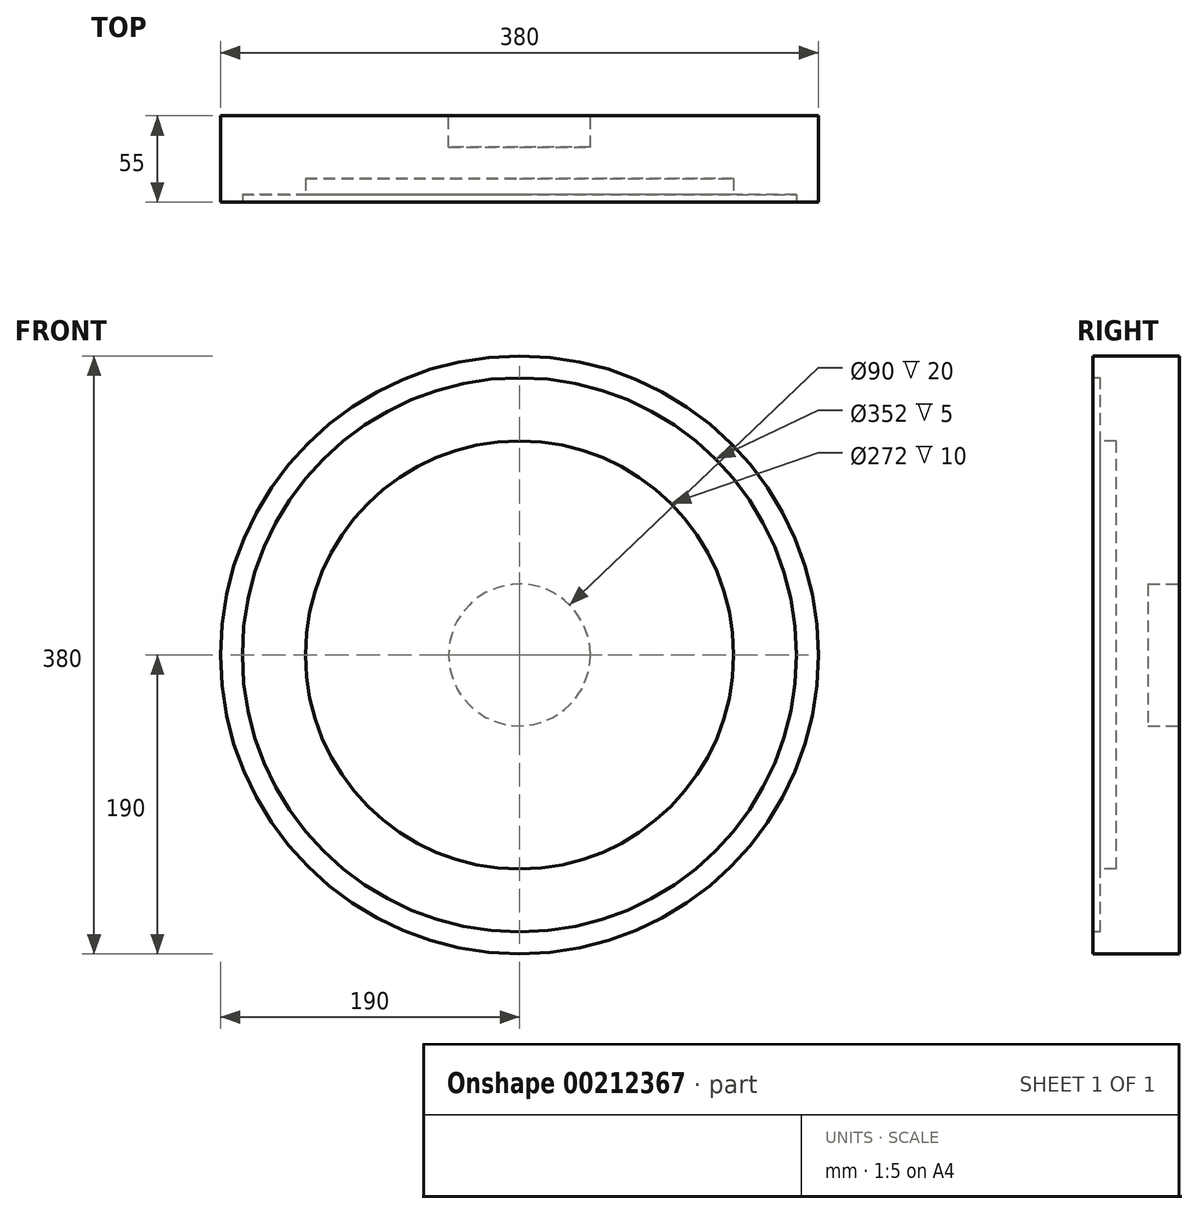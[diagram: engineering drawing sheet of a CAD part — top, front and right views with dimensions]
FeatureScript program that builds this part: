
annotation { "Feature Type Name" : "Feature", "Feature Type Description" : "" }
export const myFeature = defineFeature(function(context is Context, id is Id, definition is map)
    precondition{}
    {
        {
            var Q0;
            Q0=qCreatedBy(makeId("Front.planeOp"),FACE);
            var sketch = newSketch(context, id + "F0", { "sketchPlane" : qUnion([Q0])});
            skCircle(sketch, "E0", {"center": v(0, 0) * mm, "radius": 190 * mm});
            skSolve(sketch);
        }
        {
            var Q0;
            Q0=makeQuery(id+"F0.imprint","IMPRINT",FACE,{"disambiguationData":[TD([[makeQuery(id+"F0.imprint","IMPRINT",EDGE,{"derivedFrom":sQuery(id+"F0.wireOp",EDGE,"E0")}),1.0]])]});
            extrude(context, id + "F1", {"entities" : qUnion([Q0]), "depth" : 55 * mm});
        }
        {
            var Q0;
            Q0=makeQuery(id+"F1.opExtrude","CAP_FACE",FACE,{"disambiguationData":[OSD([sQuery(id+"F0.wireOp",EDGE,"E0")])],"isStart":true});
            var sketch = newSketch(context, id + "F2", { "sketchPlane" : qUnion([Q0])});
            skCircle(sketch, "E1", {"center": v(0, 0) * mm, "radius": 45 * mm});
            skSolve(sketch);
        }
        {
            var Q0;
            Q0=makeQuery(id+"F2.imprint","IMPRINT",FACE,{"disambiguationData":[TD([[makeQuery(id+"F2.imprint","IMPRINT",EDGE,{"derivedFrom":sQuery(id+"F2.wireOp",EDGE,"E1")}),1.0]])]});
            extrude(context, id + "F3", {"entities" : qUnion([Q0]), "operationType" : NewBodyOperationType.REMOVE, "oppositeDirection" : true, "depth" : 20 * mm});
        }
        {
            var Q0;
            Q0=makeQuery(id+"F1.opExtrude","CAP_FACE",FACE,{"disambiguationData":[OSD([sQuery(id+"F0.wireOp",EDGE,"E0")])],"isStart":false});
            var sketch = newSketch(context, id + "F4", { "sketchPlane" : qUnion([Q0])});
            skCircle(sketch, "E2", {"center": v(0, 0) * mm, "radius": 176 * mm});
            skCircle(sketch, "E3", {"center": v(0, 0) * mm, "radius": 136 * mm});
            skSolve(sketch);
        }
        {
            var Q0;
            Q0=makeQuery(id+"F4.imprint","IMPRINT",FACE,{"disambiguationData":[TD([[makeQuery(id+"F4.imprint","IMPRINT",EDGE,{"derivedFrom":sQuery(id+"F4.wireOp",EDGE,"E2")}),1.0]])]});
            extrude(context, id + "F5", {"entities" : qUnion([Q0]), "operationType" : NewBodyOperationType.REMOVE, "oppositeDirection" : true, "depth" : 5 * mm});
        }
        {
            var Q0;
            Q0=makeQuery(id+"F5.boolean.opBoolean","SPLIT",FACE,{"disambiguationData":[TD([makeQuery(id+"F5.opExtrude","SWEPT_FACE",FACE,{"disambiguationData":[OSD([sQuery(id+"F4.wireOp",EDGE,"E3")])]})])],"derivedFrom":makeQuery(id+"F1.opExtrude","CAP_FACE",FACE,{"disambiguationData":[OSD([sQuery(id+"F0.wireOp",EDGE,"E0")])],"isStart":false})});
            extrude(context, id + "F6", {"entities" : qUnion([Q0]), "operationType" : NewBodyOperationType.REMOVE, "oppositeDirection" : true, "depth" : 15 * mm});
        }
    });
